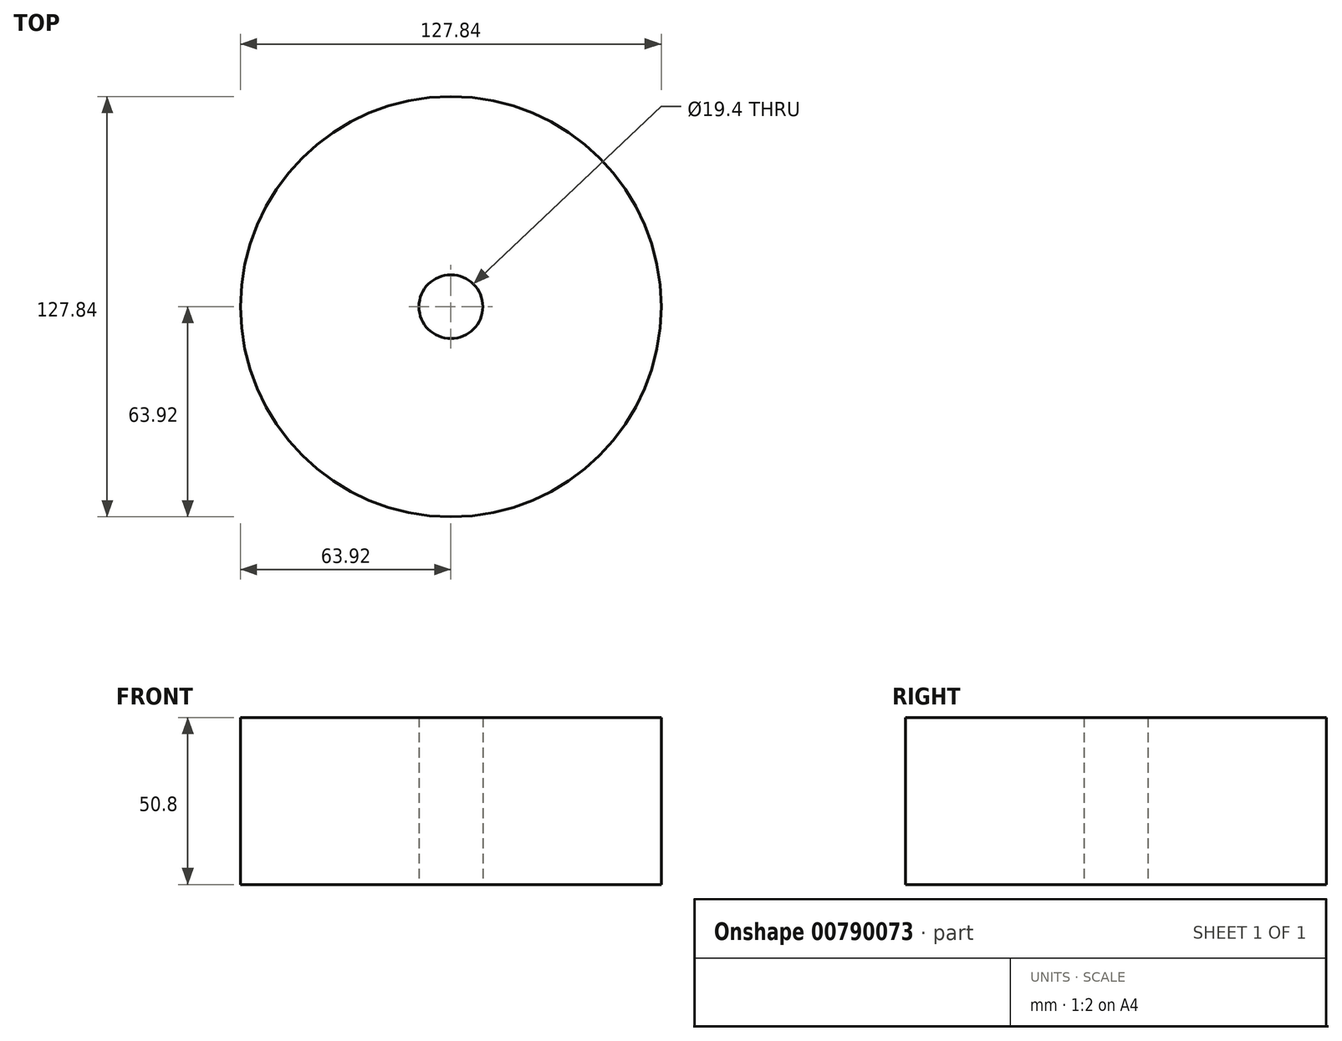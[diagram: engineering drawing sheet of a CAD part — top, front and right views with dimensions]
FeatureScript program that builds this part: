
annotation { "Feature Type Name" : "Feature", "Feature Type Description" : "" }
export const myFeature = defineFeature(function(context is Context, id is Id, definition is map)
    precondition{}
    {
        {
            var Q0;
            Q0=qCreatedBy(makeId("Top.planeOp"),FACE);
            var sketch = newSketch(context, id + "F0", { "sketchPlane" : qUnion([Q0])});
            skCircle(sketch, "E0", {"center": v(0, 0) * mm, "radius": 9.7 * mm});
            skCircle(sketch, "E1", {"center": v(0, 0) * mm, "radius": 63.92 * mm});
            skSolve(sketch);
        }
        {
            var Q0;
            Q0 = qSketchRegion(id + "F0", true);
            var Q1;
            Q1=sQuery(id+"F0.wireOp",EDGE,"E1");
            extrude(context, id + "F1", {"entities" : qUnion([Q0]), "surfaceEntities" : qUnion([Q1]), "depth" : 50.8 * mm, "offsetDistance" : 25.4 * mm});
        }
    });
